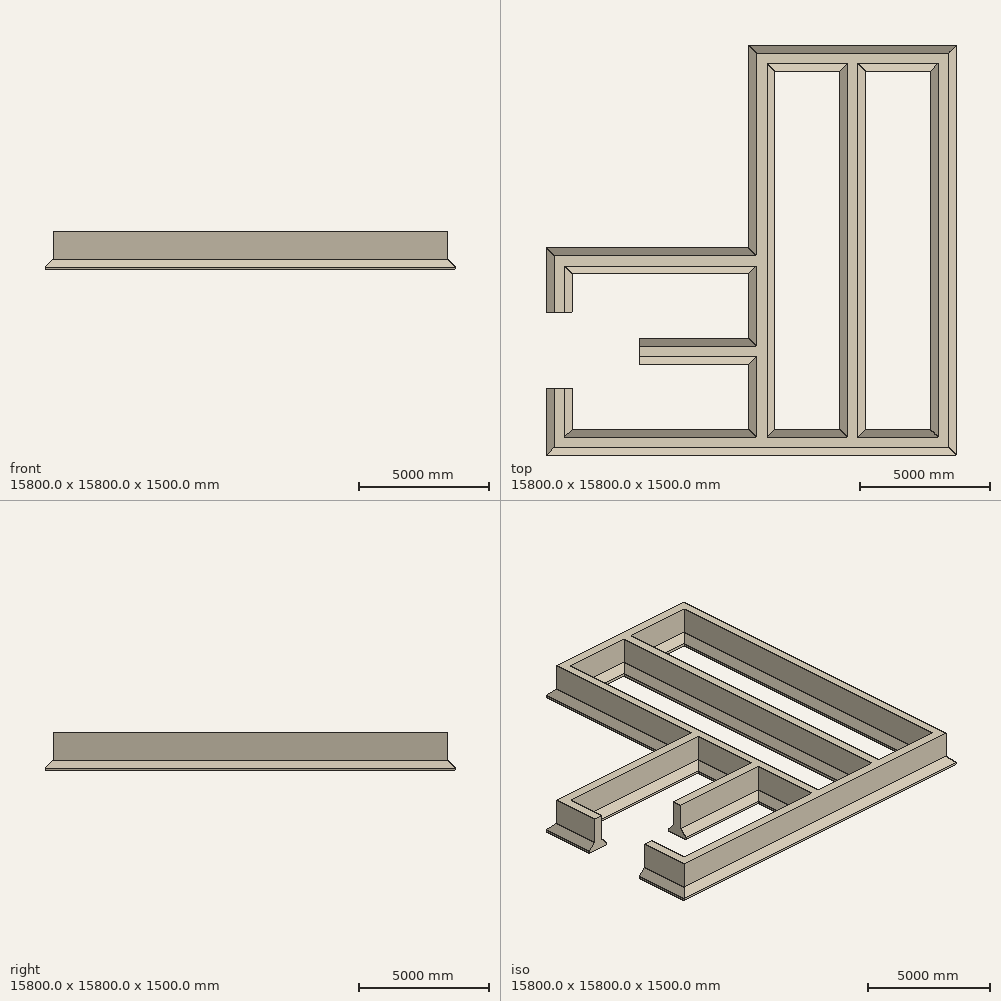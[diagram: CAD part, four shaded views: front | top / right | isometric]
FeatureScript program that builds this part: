
annotation { "Feature Type Name" : "Feature", "Feature Type Description" : "" }
export const myFeature = defineFeature(function(context is Context, id is Id, definition is map)
    precondition{}
    {
        {
            var Q0;
            Q0=qCreatedBy(makeId("Top.planeOp"),FACE);
            var sketch = newSketch(context, id + "F0", { "sketchPlane" : qUnion([Q0])});
            skLineSegment(sketch, "E0", {"start": v(0, 0) * mm, "end": v(15200, 0) * mm});
            skLineSegment(sketch, "E1", {"start": v(15200, 0) * mm, "end": v(15200, 15200) * mm});
            skLineSegment(sketch, "E2", {"start": v(15200, 15200) * mm, "end": v(7800, 15200) * mm});
            skLineSegment(sketch, "E3", {"start": v(7800, 15200) * mm, "end": v(7800, 7400) * mm});
            skLineSegment(sketch, "E4", {"start": v(7800, 7400) * mm, "end": v(0, 7400) * mm});
            skLineSegment(sketch, "E5", {"start": v(0, 7400) * mm, "end": v(0, 0) * mm});
            skLineSegment(sketch, "E6", {"start": v(400, 400) * mm, "end": v(14800, 400) * mm});
            skLineSegment(sketch, "E7", {"start": v(14800, 400) * mm, "end": v(14800, 14800) * mm});
            skLineSegment(sketch, "E8", {"start": v(14800, 14800) * mm, "end": v(8200, 14800) * mm});
            skLineSegment(sketch, "E9", {"start": v(8200, 14800) * mm, "end": v(8200, 7000) * mm});
            skLineSegment(sketch, "E10", {"start": v(8200, 7000) * mm, "end": v(400, 7000) * mm});
            skLineSegment(sketch, "E11", {"start": v(400, 7000) * mm, "end": v(400, 400) * mm});
            skLineSegment(sketch, "E12", {"start": v(8200, 7000) * mm, "end": v(8200, 400) * mm});
            skLineSegment(sketch, "E13", {"start": v(7800, 7000) * mm, "end": v(7800, 400) * mm});
            skLineSegment(sketch, "E14", {"start": v(7800, 3500) * mm, "end": v(400, 3500) * mm});
            skLineSegment(sketch, "E15", {"start": v(7800, 3900) * mm, "end": v(400, 3900) * mm});
            skLineSegment(sketch, "E16", {"start": v(11300, 14800) * mm, "end": v(11300, 400) * mm});
            skLineSegment(sketch, "E17", {"start": v(11700, 14800) * mm, "end": v(11700, 400) * mm});
            skSolve(sketch);
        }
        {
            var Q0;
            Q0 = qSketchRegion(id + "F0", true);
            var Q1;
            {var subQ4=sQuery(id+"F0.wireOp",EDGE,"E12");Q1=makeQuery(id+"F0.imprint","IMPRINT",FACE,{"disambiguationData":[TD([[makeQuery(id+"F0.imprint","IMPRINT",EDGE,{"derivedFrom":subQ4}),-1.0]])]});}
            var Q2;
            {var subQ0=sQuery(id+"F0.wireOp",EDGE,"E14");Q2=makeQuery(id+"F0.imprint","IMPRINT",FACE,{"disambiguationData":[TD([[makeQuery(id+"F0.imprint","IMPRINT",EDGE,{"derivedFrom":subQ0}),-1.0]])]});}
            var Q3;
            {var subQ0=sQuery(id+"F0.wireOp",EDGE,"E16");Q3=makeQuery(id+"F0.imprint","IMPRINT",FACE,{"disambiguationData":[TD([[makeQuery(id+"F0.imprint","IMPRINT",EDGE,{"derivedFrom":subQ0}),1.0]])]});}
            extrude(context, id + "F1", {"entities" : qUnion([Q0, Q1, Q2, Q3]), "depth" : 1500 * mm});
        }
        {
            var Q0;
            Q0=makeQuery(id+"F1.opExtrude","CAP_FACE",FACE,{"disambiguationData":[OSD([sQuery(id+"F0.wireOp",EDGE,"E0"),sQuery(id+"F0.wireOp",EDGE,"E1"),sQuery(id+"F0.wireOp",EDGE,"E2"),sQuery(id+"F0.wireOp",EDGE,"E3"),sQuery(id+"F0.wireOp",EDGE,"E4"),sQuery(id+"F0.wireOp",EDGE,"E5"),sQuery(id+"F0.wireOp",EDGE,"E6"),sQuery(id+"F0.wireOp",EDGE,"E7"),sQuery(id+"F0.wireOp",EDGE,"E8"),sQuery(id+"F0.wireOp",EDGE,"E9"),sQuery(id+"F0.wireOp",EDGE,"E10"),sQuery(id+"F0.wireOp",EDGE,"E11")])],"isStart":true});
            var sketch = newSketch(context, id + "F2", { "sketchPlane" : qUnion([Q0])});
            skLineSegment(sketch, "E18.bottom", {"start": v(700, -700) * mm, "end": v(7500, -700) * mm});
            skLineSegment(sketch, "E18.top", {"start": v(700, -3200) * mm, "end": v(7500, -3200) * mm});
            skLineSegment(sketch, "E18.left", {"start": v(700, -700) * mm, "end": v(700, -3200) * mm});
            skLineSegment(sketch, "E18.right", {"start": v(7500, -700) * mm, "end": v(7500, -3200) * mm});
            skLineSegment(sketch, "E19.bottom", {"start": v(700, -4200) * mm, "end": v(7500, -4200) * mm});
            skLineSegment(sketch, "E19.top", {"start": v(700, -6700) * mm, "end": v(7500, -6700) * mm});
            skLineSegment(sketch, "E19.left", {"start": v(700, -4200) * mm, "end": v(700, -6700) * mm});
            skLineSegment(sketch, "E19.right", {"start": v(7500, -4200) * mm, "end": v(7500, -6700) * mm});
            skPoint(sketch, "E20.firstSnap0", {"position": v(4100, -700) * mm});
            skLineSegment(sketch, "E20.bottom", {"start": v(8500, -700) * mm, "end": v(14500, -700) * mm});
            skLineSegment(sketch, "E20.top", {"start": v(8500, -14500) * mm, "end": v(14500, -14500) * mm});
            skLineSegment(sketch, "E20.left", {"start": v(8500, -700) * mm, "end": v(8500, -14500) * mm});
            skLineSegment(sketch, "E20.right", {"start": v(14500, -700) * mm, "end": v(14500, -14500) * mm});
            skLineSegment(sketch, "E21", {"start": v(-300, 300) * mm, "end": v(-300, -7700) * mm});
            skLineSegment(sketch, "E22", {"start": v(-300, -7700) * mm, "end": v(7500, -7700) * mm});
            skLineSegment(sketch, "E23", {"start": v(7500, -7700) * mm, "end": v(7500, -15500) * mm});
            skLineSegment(sketch, "E24", {"start": v(7500, -15500) * mm, "end": v(15500, -15500) * mm});
            skLineSegment(sketch, "E25", {"start": v(15500, -15500) * mm, "end": v(15500, 300) * mm});
            skLineSegment(sketch, "E26", {"start": v(15500, 300) * mm, "end": v(-300, 300) * mm});
            skLineSegment(sketch, "E27", {"start": v(11000, -700) * mm, "end": v(11000, -14500) * mm});
            skLineSegment(sketch, "E28", {"start": v(12000, -14500) * mm, "end": v(12000, -700) * mm});
            skSolve(sketch);
        }
        {
            var Q0;
            Q0 = qSketchRegion(id + "F2", true);
            var Q1;
            {var subQ0=sQuery(id+"F2.wireOp",EDGE,"E27");Q1=makeQuery(id+"F2.imprint","IMPRINT",FACE,{"disambiguationData":[TD([[makeQuery(id+"F2.imprint","IMPRINT",EDGE,{"derivedFrom":subQ0}),1.0]])]});}
            var Q2;
            {var subQ0=sQuery(id+"F2.wireOp",EDGE,"E20.bottom");var subQ1=makeQuery(id+"F1.opExtrude","CAP_EDGE",EDGE,{"disambiguationData":[OSD([sQuery(id+"F0.wireOp",EDGE,"E16")])],"isStart":true});var subQ2=makeQuery(id+"F2.imprint","INTERSECT",VERTEX,{"derivedFrom":[subQ1,subQ0]});Q2=makeQuery(id+"F2.imprint","IMPRINT",FACE,{"disambiguationData":[TD([[makeQuery(id+"F2.imprint","IMPRINT",EDGE,{"disambiguationData":[TD([[subQ2,-1.0]])],"derivedFrom":subQ0}),-1.0]])]});}
            var Q3;
            {var subQ0=sQuery(id+"F2.wireOp",EDGE,"E28");Q3=makeQuery(id+"F2.imprint","IMPRINT",FACE,{"disambiguationData":[TD([[makeQuery(id+"F2.imprint","IMPRINT",EDGE,{"derivedFrom":subQ0}),1.0]])]});}
            extrude(context, id + "F3", {"entities" : qUnion([Q0, Q1, Q2, Q3]), "operationType" : NewBodyOperationType.ADD, "oppositeDirection" : true, "depth" : 400 * mm});
        }
        {
            var Q0;
            Q0=makeQuery(id+"F3.opExtrude","CAP_EDGE",EDGE,{"disambiguationData":[OSD([sQuery(id+"F2.wireOp",EDGE,"E26")])],"isStart":false});
            var Q1;
            Q1=makeQuery(id+"F3.opExtrude","CAP_EDGE",EDGE,{"disambiguationData":[OSD([sQuery(id+"F2.wireOp",EDGE,"E21")])],"isStart":false});
            var Q2;
            Q2=makeQuery(id+"F3.opExtrude","CAP_EDGE",EDGE,{"disambiguationData":[OSD([sQuery(id+"F2.wireOp",EDGE,"E25")])],"isStart":false});
            var Q3;
            Q3=makeQuery(id+"F3.opExtrude","CAP_EDGE",EDGE,{"disambiguationData":[OSD([sQuery(id+"F2.wireOp",EDGE,"E24")])],"isStart":false});
            var Q4;
            Q4=makeQuery(id+"F3.opExtrude","CAP_EDGE",EDGE,{"disambiguationData":[OSD([sQuery(id+"F2.wireOp",EDGE,"E20.left")])],"isStart":false});
            var Q5;
            Q5=makeQuery(id+"F3.opExtrude","CAP_EDGE",EDGE,{"disambiguationData":[OSD([sQuery(id+"F2.wireOp",EDGE,"E20.bottom")])],"isStart":false});
            var Q6;
            Q6=makeQuery(id+"F3.opExtrude","CAP_EDGE",EDGE,{"disambiguationData":[OSD([sQuery(id+"F2.wireOp",EDGE,"E20.right")])],"isStart":false});
            var Q7;
            Q7=makeQuery(id+"F3.opExtrude","CAP_EDGE",EDGE,{"disambiguationData":[OSD([sQuery(id+"F2.wireOp",EDGE,"E20.top")])],"isStart":false});
            var Q8;
            Q8=makeQuery(id+"F3.opExtrude","CAP_EDGE",EDGE,{"disambiguationData":[OSD([sQuery(id+"F2.wireOp",EDGE,"E23")])],"isStart":false});
            var Q9;
            Q9=makeQuery(id+"F3.opExtrude","CAP_EDGE",EDGE,{"disambiguationData":[OSD([sQuery(id+"F2.wireOp",EDGE,"E22")])],"isStart":false});
            var Q10;
            Q10=makeQuery(id+"F3.opExtrude","CAP_EDGE",EDGE,{"disambiguationData":[OSD([sQuery(id+"F2.wireOp",EDGE,"E19.bottom")])],"isStart":false});
            var Q11;
            Q11=makeQuery(id+"F3.opExtrude","CAP_EDGE",EDGE,{"disambiguationData":[OSD([sQuery(id+"F2.wireOp",EDGE,"E18.bottom")])],"isStart":false});
            var Q12;
            Q12=makeQuery(id+"F3.opExtrude","CAP_EDGE",EDGE,{"disambiguationData":[OSD([sQuery(id+"F2.wireOp",EDGE,"E18.right")])],"isStart":false});
            var Q13;
            Q13=makeQuery(id+"F3.opExtrude","CAP_EDGE",EDGE,{"disambiguationData":[OSD([sQuery(id+"F2.wireOp",EDGE,"E19.right")])],"isStart":false});
            var Q14;
            Q14=makeQuery(id+"F3.opExtrude","CAP_EDGE",EDGE,{"disambiguationData":[OSD([sQuery(id+"F2.wireOp",EDGE,"E18.left")])],"isStart":false});
            var Q15;
            Q15=makeQuery(id+"F3.opExtrude","CAP_EDGE",EDGE,{"disambiguationData":[OSD([sQuery(id+"F2.wireOp",EDGE,"E19.left")])],"isStart":false});
            var Q16;
            Q16=makeQuery(id+"F3.opExtrude","CAP_EDGE",EDGE,{"disambiguationData":[OSD([sQuery(id+"F2.wireOp",EDGE,"E18.top")])],"isStart":false});
            var Q17;
            Q17=makeQuery(id+"F3.opExtrude","CAP_EDGE",EDGE,{"disambiguationData":[OSD([sQuery(id+"F2.wireOp",EDGE,"E19.top")])],"isStart":false});
            var Q18;
            Q18=makeQuery(id+"F3.opExtrude","CAP_EDGE",EDGE,{"disambiguationData":[OSD([sQuery(id+"F2.wireOp",EDGE,"E27")])],"isStart":false});
            var Q19;
            Q19=makeQuery(id+"F3.opExtrude","CAP_EDGE",EDGE,{"disambiguationData":[OSD([sQuery(id+"F2.wireOp",EDGE,"E28")])],"isStart":false});
            chamfer(context, id + "F4", {"entities" : qUnion([Q0, Q1, Q2, Q3, Q4, Q5, Q6, Q7, Q8, Q9, Q10, Q11, Q12, Q13, Q14, Q15, Q16, Q17, Q18, Q19]), "width" : 300 * mm, "tangentPropagation" : true});
        }
        {
            var Q0;
            Q0=makeQuery(id+"F1.opExtrude","CAP_FACE",FACE,{"disambiguationData":[OSD([sQuery(id+"F0.wireOp",EDGE,"E0"),sQuery(id+"F0.wireOp",EDGE,"E1"),sQuery(id+"F0.wireOp",EDGE,"E2"),sQuery(id+"F0.wireOp",EDGE,"E3"),sQuery(id+"F0.wireOp",EDGE,"E4"),sQuery(id+"F0.wireOp",EDGE,"E5"),sQuery(id+"F0.wireOp",EDGE,"E6"),sQuery(id+"F0.wireOp",EDGE,"E7"),sQuery(id+"F0.wireOp",EDGE,"E8"),sQuery(id+"F0.wireOp",EDGE,"E9"),sQuery(id+"F0.wireOp",EDGE,"E10"),sQuery(id+"F0.wireOp",EDGE,"E11"),sQuery(id+"F0.wireOp",EDGE,"E12"),sQuery(id+"F0.wireOp",EDGE,"E13"),sQuery(id+"F0.wireOp",EDGE,"E14"),sQuery(id+"F0.wireOp",EDGE,"E15"),sQuery(id+"F0.wireOp",EDGE,"E16"),sQuery(id+"F0.wireOp",EDGE,"E17")])],"isStart":false});
            var sketch = newSketch(context, id + "F5", { "sketchPlane" : qUnion([Q0])});
            skLineSegment(sketch, "E29.bottom", {"start": v(3300, 5200) * mm, "end": v(-300, 5200) * mm});
            skLineSegment(sketch, "E29.top", {"start": v(3300, 2300) * mm, "end": v(-300, 2300) * mm});
            skLineSegment(sketch, "E29.left", {"start": v(3300, 5200) * mm, "end": v(3300, 2300) * mm});
            skLineSegment(sketch, "E29.right", {"start": v(-300, 5200) * mm, "end": v(-300, 2300) * mm});
            skSolve(sketch);
        }
        {
            var Q0;
            Q0 = qSketchRegion(id + "F5", true);
            extrude(context, id + "F6", {"entities" : qUnion([Q0]), "operationType" : NewBodyOperationType.REMOVE, "endBound" : BoundingType.THROUGH_ALL, "oppositeDirection" : true, "depth" : 25 * mm, "offsetDistance" : 25 * mm});
        }
    });
